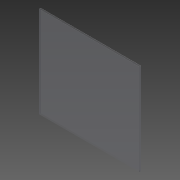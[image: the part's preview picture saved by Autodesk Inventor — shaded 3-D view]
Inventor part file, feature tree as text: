
AUTODESK INVENTOR PART (.ipt)
format: ipt  version: 2013 (Build 170138000, 138)  size: 110,592 bytes
history: native  units: in
note: dims shown in document units (in); Inventor stores cm internally (conversion verified against a paired STEP export)
features: sheet_metal_op x7, sketch x3, other x3
ambient origin geometry x8: Origin, YZ Plane, XZ Plane, XY Plane, X Axis, Y Axis, Z Axis, Center Point
bodies: Solid1 (feature_tree)
feature tree (13):
  sheet_metal_op  "Face1"
  sheet_metal_op  "Flange1"
  sheet_metal_op  "Flange2"
  sketch  "Sketch1"  dims[d0=53.0in]
  other  "Plate1"
  sketch  "Sketch2"  dims[d1=48.0in]
  other  "Plate2"
  sheet_metal_op  "Bend1"
  sheet_metal_op  "Corner1"
  sketch  "Sketch3"  dims[d2=0.12in d3=0.12in d4=0.06in d5=0.24in d6=0.12in d7=1.0in d8=90.0deg d9=0.12in d10=0.48in d11=0.12in d12=0.12in d13=0.12in d14=0.06in d15=0.24in d16=0.12in d17=26.5in d18=90.0deg d19=0.12in d20=0.48in d21=0.12in d22=0.12in]
  other  "Plate3"
  sheet_metal_op  "Bend2"
  sheet_metal_op  "Corner2"
